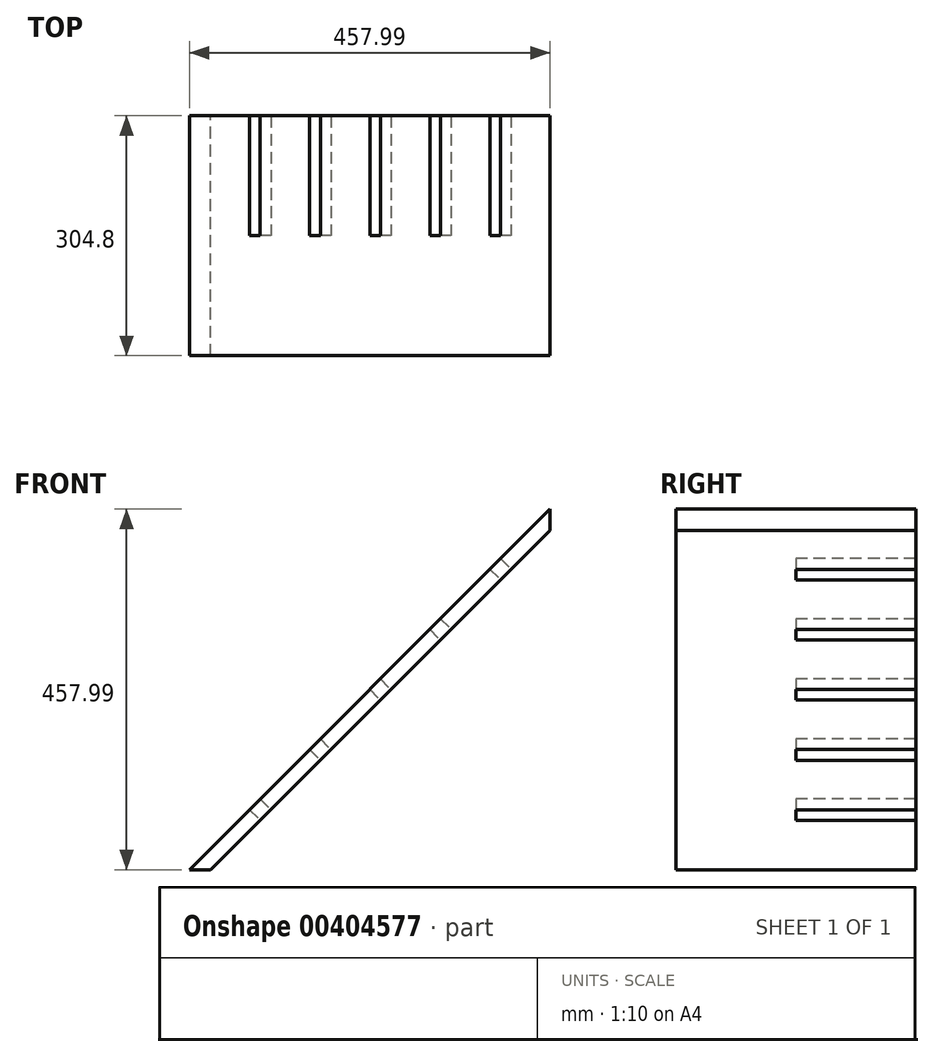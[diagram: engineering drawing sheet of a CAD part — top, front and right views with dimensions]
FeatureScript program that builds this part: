
annotation { "Feature Type Name" : "Feature", "Feature Type Description" : "" }
export const myFeature = defineFeature(function(context is Context, id is Id, definition is map)
    precondition{}
    {
        {
            var Q0;
            Q0=qCreatedBy(makeId("Front.planeOp"),FACE);
            var sketch = newSketch(context, id + "F0", { "sketchPlane" : qUnion([Q0])});
            skLineSegment(sketch, "E0", {"start": v(-337.22, 0) * mm, "end": v(120.77, 458) * mm});
            skPoint(sketch, "E1.MirrorP", {"position": v(53.93, 355.6) * mm});
            skLineSegment(sketch, "E2.MirrorCS", {"start": v(-310.28, 0) * mm, "end": v(120.77, 431.05) * mm});
            skLineSegment(sketch, "E3", {"start": v(-310.28, 0) * mm, "end": v(-337.22, 0) * mm});
            skLineSegment(sketch, "E4", {"start": v(120.77, 458) * mm, "end": v(120.77, 431.05) * mm});
            skSolve(sketch);
        }
        {
            var Q0;
            Q0=qSketchRegion(id+"F0",true);
            extrude(context, id + "F1", {"entities" : qUnion([Q0]), "endBound" : BoundingType.SYMMETRIC, "depth" : 304.8 * mm});
        }
        {
            var Q0;
            Q0=makeQuery(id+"F1.opExtrude","SWEPT_FACE",FACE,{"disambiguationData":[OSD([sQuery(id+"F0.wireOp",EDGE,"E2.MirrorCS")])]});
            var sketch = newSketch(context, id + "F2", { "sketchPlane" : qUnion([Q0])});
            skLineSegment(sketch, "E5.bottom", {"start": v(152.4, 320.35) * mm, "end": v(0, 320.35) * mm});
            skLineSegment(sketch, "E5.top", {"start": v(152.4, 301.3) * mm, "end": v(0, 301.3) * mm});
            skLineSegment(sketch, "E5.left", {"start": v(152.4, 320.35) * mm, "end": v(152.4, 301.3) * mm});
            skLineSegment(sketch, "E5.right", {"start": v(0, 320.35) * mm, "end": v(0, 301.3) * mm});
            skLineSegment(sketch, "E6.bottom", {"start": v(152.4, 212.4) * mm, "end": v(0, 212.4) * mm});
            skLineSegment(sketch, "E6.top", {"start": v(152.4, 193.35) * mm, "end": v(0, 193.35) * mm});
            skLineSegment(sketch, "E6.left", {"start": v(152.4, 212.4) * mm, "end": v(152.4, 193.35) * mm});
            skLineSegment(sketch, "E6.right", {"start": v(0, 212.4) * mm, "end": v(0, 193.35) * mm});
            skLineSegment(sketch, "E7.bottom", {"start": v(152.4, 104.45) * mm, "end": v(0, 104.45) * mm});
            skLineSegment(sketch, "E7.top", {"start": v(152.4, 85.4) * mm, "end": v(0, 85.4) * mm});
            skLineSegment(sketch, "E7.left", {"start": v(152.4, 104.45) * mm, "end": v(152.4, 85.4) * mm});
            skLineSegment(sketch, "E7.right", {"start": v(0, 104.45) * mm, "end": v(0, 85.4) * mm});
            skLineSegment(sketch, "E8.bottom", {"start": v(152.4, -3.5) * mm, "end": v(0, -3.5) * mm});
            skLineSegment(sketch, "E8.top", {"start": v(152.4, -22.55) * mm, "end": v(0, -22.55) * mm});
            skLineSegment(sketch, "E8.left", {"start": v(152.4, -3.5) * mm, "end": v(152.4, -22.55) * mm});
            skLineSegment(sketch, "E8.right", {"start": v(0, -3.5) * mm, "end": v(0, -22.55) * mm});
            skLineSegment(sketch, "E9.bottom", {"start": v(152.4, -111.45) * mm, "end": v(0, -111.45) * mm});
            skLineSegment(sketch, "E9.top", {"start": v(152.4, -130.5) * mm, "end": v(0, -130.5) * mm});
            skLineSegment(sketch, "E9.left", {"start": v(152.4, -111.45) * mm, "end": v(152.4, -130.5) * mm});
            skLineSegment(sketch, "E9.right", {"start": v(0, -111.45) * mm, "end": v(0, -130.5) * mm});
            skSolve(sketch);
        }
        {
            var Q0;
            Q0=qSketchRegion(id+"F2",true);
            extrude(context, id + "F3", {"entities" : qUnion([Q0]), "operationType" : NewBodyOperationType.REMOVE, "oppositeDirection" : true, "depth" : 19.05 * mm});
        }
    });
